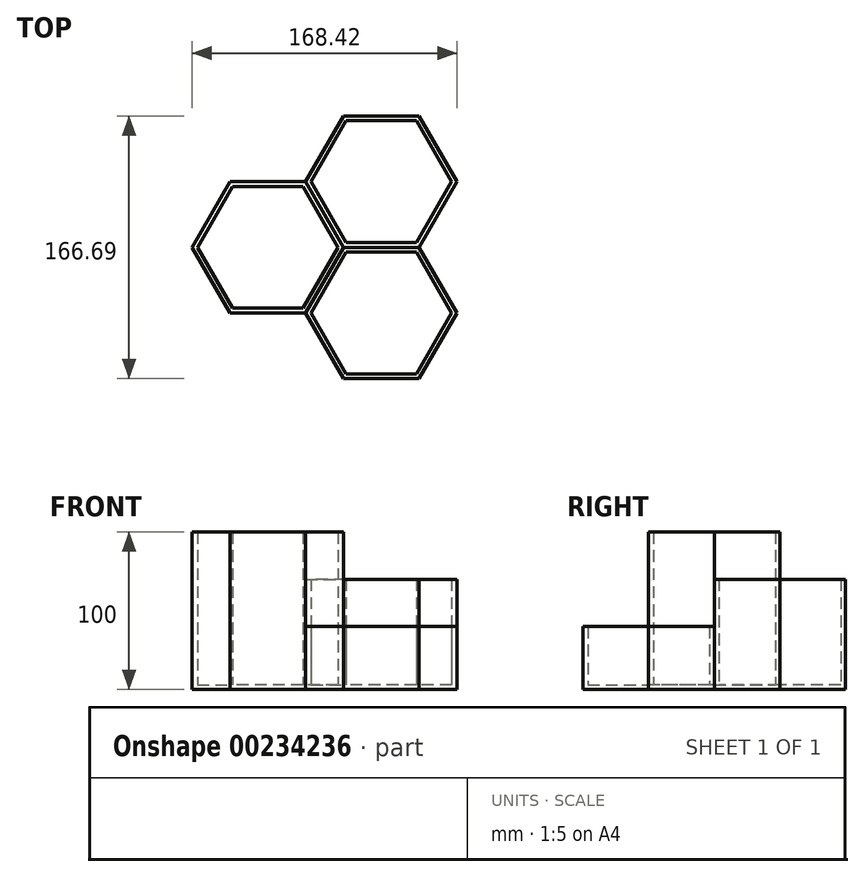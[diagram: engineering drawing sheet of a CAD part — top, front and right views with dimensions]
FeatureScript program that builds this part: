
annotation { "Feature Type Name" : "Feature", "Feature Type Description" : "" }
export const myFeature = defineFeature(function(context is Context, id is Id, definition is map)
    precondition{}
    {
        {
            var Q0;
            Q0=qCreatedBy(makeId("Top.planeOp"),FACE);
            var sketch = newSketch(context, id + "F0", { "sketchPlane" : qUnion([Q0])});
            skCircle(sketch, "E0.cCircle", {"center": v(0, 0) * mm, "radius": 41.67 * mm, "construction": true});
            skLineSegment(sketch, "E0.0", {"start": v(24.06, -41.67) * mm, "end": v(-24.06, -41.67) * mm});
            skLineSegment(sketch, "E0.1", {"start": v(-24.06, -41.67) * mm, "end": v(-48.12, 0) * mm});
            skLineSegment(sketch, "E0.2", {"start": v(-48.12, 0) * mm, "end": v(-24.06, 41.67) * mm});
            skLineSegment(sketch, "E0.3", {"start": v(-24.06, 41.67) * mm, "end": v(24.06, 41.67) * mm});
            skLineSegment(sketch, "E0.4", {"start": v(24.06, 41.67) * mm, "end": v(48.12, 0) * mm});
            skLineSegment(sketch, "E0.5", {"start": v(48.12, 0) * mm, "end": v(24.06, -41.67) * mm});
            skPoint(sketch, "E0.0.midPoint", {"position": v(0, -41.67) * mm});
            skCircle(sketch, "E1.cCircle", {"center": v(-72.18, -41.67) * mm, "radius": 41.67 * mm, "construction": true});
            skLineSegment(sketch, "E1.0", {"start": v(-48.12, -83.35) * mm, "end": v(-96.24, -83.35) * mm});
            skLineSegment(sketch, "E1.1", {"start": v(-96.24, -83.35) * mm, "end": v(-120.3, -41.67) * mm});
            skLineSegment(sketch, "E1.2", {"start": v(-120.3, -41.67) * mm, "end": v(-96.24, 0) * mm});
            skLineSegment(sketch, "E1.3", {"start": v(-96.24, 0) * mm, "end": v(-48.12, 0) * mm});
            skLineSegment(sketch, "E1.4", {"start": v(-48.12, 0) * mm, "end": v(-24.06, -41.67) * mm});
            skLineSegment(sketch, "E1.5", {"start": v(-24.06, -41.67) * mm, "end": v(-48.12, -83.35) * mm});
            skPoint(sketch, "E1.0.midPoint", {"position": v(-72.18, -83.35) * mm});
            skCircle(sketch, "E2.cCircle", {"center": v(0, -83.35) * mm, "radius": 41.67 * mm, "construction": true});
            skLineSegment(sketch, "E2.0", {"start": v(48.12, -83.35) * mm, "end": v(24.06, -125.02) * mm});
            skLineSegment(sketch, "E2.1", {"start": v(24.06, -125.02) * mm, "end": v(-24.06, -125.02) * mm});
            skLineSegment(sketch, "E2.2", {"start": v(-24.06, -125.02) * mm, "end": v(-48.12, -83.35) * mm});
            skLineSegment(sketch, "E2.3", {"start": v(-48.12, -83.35) * mm, "end": v(-24.06, -41.67) * mm});
            skLineSegment(sketch, "E2.4", {"start": v(-24.06, -41.67) * mm, "end": v(24.06, -41.67) * mm});
            skLineSegment(sketch, "E2.5", {"start": v(24.06, -41.67) * mm, "end": v(48.12, -83.35) * mm});
            skPoint(sketch, "E2.0.midPoint", {"position": v(36.1, -104.19) * mm});
            skSolve(sketch);
        }
        {
            var Q0;
            Q0=makeQuery(id+"F0.imprint","IMPRINT",FACE,{"disambiguationData":[TD([[makeQuery(id+"F0.imprint","IMPRINT",EDGE,{"derivedFrom":sQuery(id+"F0.wireOp",EDGE,"E1.0")}),-1.0]])]});
            extrude(context, id + "F1", {"entities" : qUnion([Q0]), "depth" : 100 * mm});
        }
        {
            var Q0;
            Q0=makeQuery(id+"F0.imprint","IMPRINT",FACE,{"disambiguationData":[TD([[makeQuery(id+"F0.imprint","IMPRINT",EDGE,{"derivedFrom":sQuery(id+"F0.wireOp",EDGE,"E0.2")}),-1.0]])]});
            extrude(context, id + "F2", {"entities" : qUnion([Q0]), "depth" : 70 * mm});
        }
        {
            var Q0;
            Q0=makeQuery(id+"F0.imprint","IMPRINT",FACE,{"disambiguationData":[TD([[makeQuery(id+"F0.imprint","IMPRINT",EDGE,{"derivedFrom":sQuery(id+"F0.wireOp",EDGE,"E2.0")}),-1.0]])]});
            extrude(context, id + "F3", {"entities" : qUnion([Q0]), "depth" : 40 * mm});
        }
        {
            var Q0;
            Q0=makeQuery(id+"F1.opExtrude","CAP_FACE",FACE,{"disambiguationData":[OSD([sQuery(id+"F0.wireOp",EDGE,"E1.0"),sQuery(id+"F0.wireOp",EDGE,"E1.1"),sQuery(id+"F0.wireOp",EDGE,"E1.2"),sQuery(id+"F0.wireOp",EDGE,"E1.3"),sQuery(id+"F0.wireOp",EDGE,"E1.4"),sQuery(id+"F0.wireOp",EDGE,"E2.3")])],"isStart":false});
            var Q1;
            Q1=makeQuery(id+"F2.opExtrude","CAP_FACE",FACE,{"disambiguationData":[OSD([sQuery(id+"F0.wireOp",EDGE,"E0.2"),sQuery(id+"F0.wireOp",EDGE,"E0.3"),sQuery(id+"F0.wireOp",EDGE,"E0.4"),sQuery(id+"F0.wireOp",EDGE,"E0.5"),sQuery(id+"F0.wireOp",EDGE,"E1.4"),sQuery(id+"F0.wireOp",EDGE,"E2.4")])],"isStart":false});
            shell(context, id + "F4", {"entities" : qUnion([Q0, Q1]), "thickness" : 3 * mm});
        }
        {
            var Q0;
            Q0=makeQuery(id+"F3.opExtrude","CAP_FACE",FACE,{"disambiguationData":[OSD([sQuery(id+"F0.wireOp",EDGE,"E2.0"),sQuery(id+"F0.wireOp",EDGE,"E2.1"),sQuery(id+"F0.wireOp",EDGE,"E2.2"),sQuery(id+"F0.wireOp",EDGE,"E2.3"),sQuery(id+"F0.wireOp",EDGE,"E2.4"),sQuery(id+"F0.wireOp",EDGE,"E2.5")])],"isStart":false});
            shell(context, id + "F5", {"entities" : qUnion([Q0]), "thickness" : 3 * mm});
        }
    });
